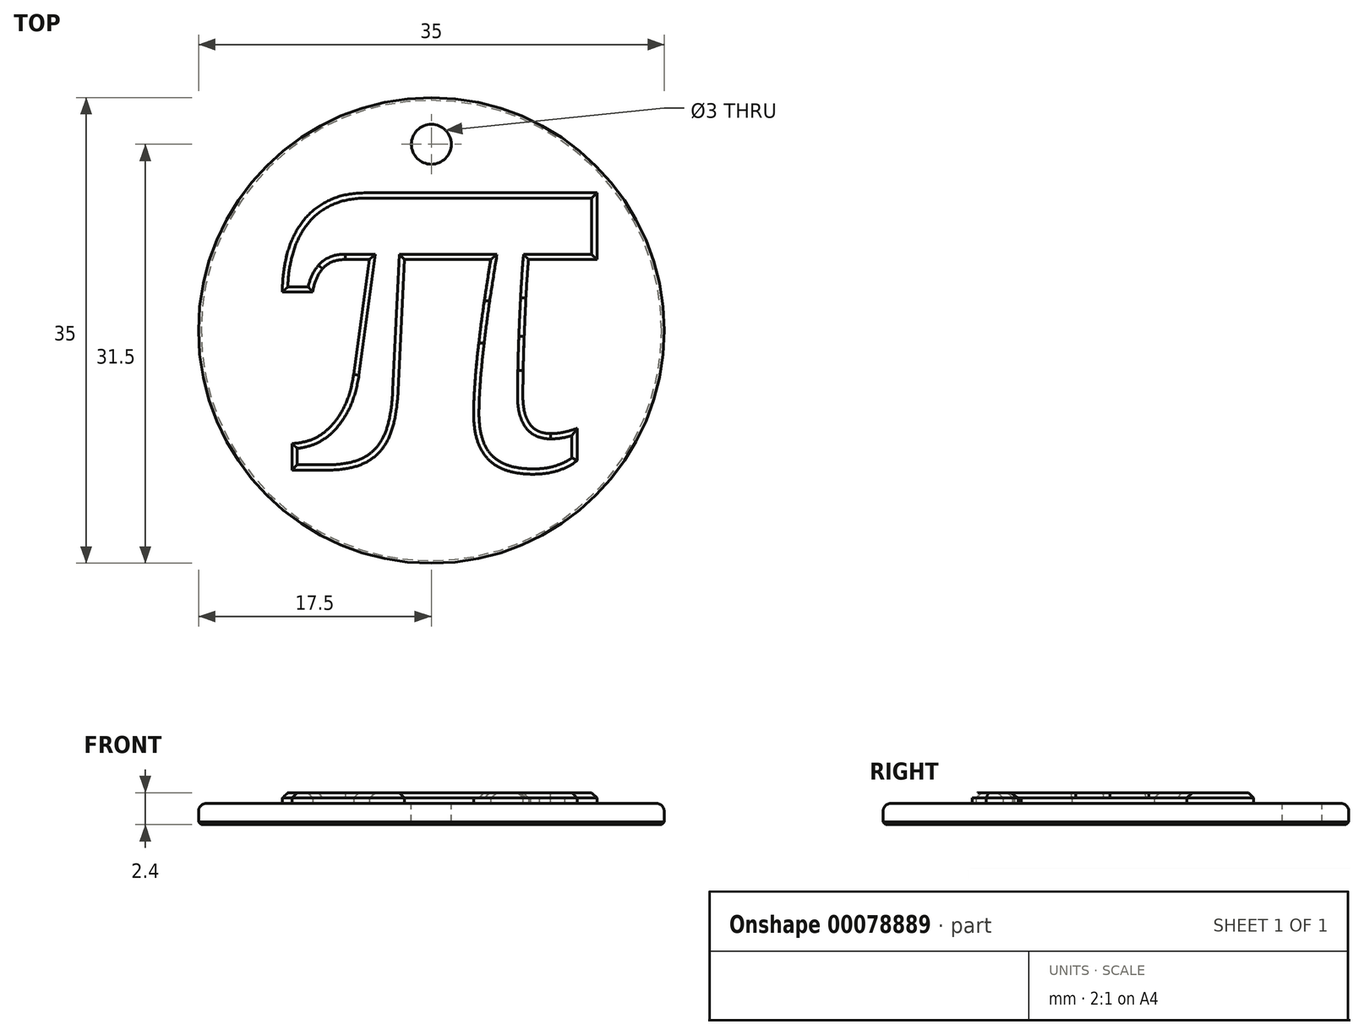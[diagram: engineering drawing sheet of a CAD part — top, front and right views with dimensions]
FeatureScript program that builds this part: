
annotation { "Feature Type Name" : "Feature", "Feature Type Description" : "" }
export const myFeature = defineFeature(function(context is Context, id is Id, definition is map)
    precondition{}
    {
        {
            var Q0;
            Q0=qCreatedBy(makeId("Top.planeOp"),FACE);
            var sketch = newSketch(context, id + "F0", { "sketchPlane" : qUnion([Q0])});
            skText(sketch, "E0", { "text": "π", "fontName": "NotoSerif-Bold.ttf"});
            skPoint(sketch, "E1", {"position": v(0, 3.5) * mm});
            skCircle(sketch, "E2", {"center": v(0, 0) * mm, "radius": 17.5 * mm});
            const initialGuessF0  = {"E0": [-0.01245, -0.0105, 1, 0, 0.028]};
            skSetInitialGuess(sketch, initialGuessF0);
            skSolve(sketch);
        }
        {
            var Q0;
            Q0 = qSketchRegion(id + "F0", true);
            var Q1;
            Q1=makeQuery(id+"F0.imprint","IMPRINT",FACE,{"disambiguationData":[TD([[makeQuery(id+"F0.imprint","IMPRINT",EDGE,{"derivedFrom":sQuery(id+"F0.wireOp",EDGE,"E0.sketch_text.stroke-0")}),-1.0]])]});
            extrude(context, id + "F1", {"entities" : qUnion([Q0, Q1]), "depth" : 1.6 * mm});
        }
        {
            var Q0;
            Q0=makeQuery(id+"F0.imprint","IMPRINT",FACE,{"disambiguationData":[TD([[makeQuery(id+"F0.imprint","IMPRINT",EDGE,{"derivedFrom":sQuery(id+"F0.wireOp",EDGE,"E0.sketch_text.stroke-0")}),-1.0]])]});
            extrude(context, id + "F2", {"entities" : qUnion([Q0]), "operationType" : NewBodyOperationType.ADD, "depth" : 2.4 * mm});
        }
        {
            var Q0;
            Q0=makeQuery(id+"F1.opExtrude","CAP_FACE",FACE,{"disambiguationData":[OSD([sQuery(id+"F0.wireOp",EDGE,"E2")])],"isStart":false});
            var sketch = newSketch(context, id + "F3", { "sketchPlane" : qUnion([Q0])});
            skCircle(sketch, "E3", {"center": v(0, 14) * mm, "radius": 1.5 * mm});
            skLineSegment(sketch, "E4", {"start": v(-7.86, 17.5) * mm, "end": v(8.67, 17.5) * mm, "construction": true});
            skSolve(sketch);
        }
        {
            var Q0;
            Q0=makeQuery(id+"F3.imprint","IMPRINT",FACE,{"disambiguationData":[TD([[makeQuery(id+"F3.imprint","IMPRINT",EDGE,{"derivedFrom":sQuery(id+"F3.wireOp",EDGE,"E3")}),1.0]])]});
            extrude(context, id + "F4", {"entities" : qUnion([Q0]), "operationType" : NewBodyOperationType.REMOVE, "endBound" : BoundingType.THROUGH_ALL, "oppositeDirection" : true, "depth" : 25 * mm});
        }
        {
            var Q0;
            Q0=makeQuery(id+"F4.boolean.opBoolean","COPY",EDGE,{"derivedFrom":makeQuery(id+"F4.opExtrude","CAP_EDGE",EDGE,{"disambiguationData":[OSD([sQuery(id+"F3.wireOp",EDGE,"E3")])],"isStart":true})});
            var Q1;
            Q1=makeQuery(id+"F1.opExtrude","CAP_EDGE",EDGE,{"disambiguationData":[OSD([sQuery(id+"F0.wireOp",EDGE,"E2")])],"isStart":false});
            fillet(context, id + "F5", {"entities" : qUnion([Q0, Q1]), "radius" : 0.6 * mm, "tangentPropagation" : true, "allowEdgeOverflow" : false});
        }
        {
            var Q0;
            Q0=makeQuery(id+"F2.opExtrude","CAP_FACE",FACE,{"disambiguationData":[OSD([sQuery(id+"F0.wireOp",EDGE,"E0.sketch_text.stroke-0"),sQuery(id+"F0.wireOp",EDGE,"E0.sketch_text.stroke-1"),sQuery(id+"F0.wireOp",EDGE,"E0.sketch_text.stroke-2"),sQuery(id+"F0.wireOp",EDGE,"E0.sketch_text.stroke-3"),sQuery(id+"F0.wireOp",EDGE,"E0.sketch_text.stroke-4"),sQuery(id+"F0.wireOp",EDGE,"E0.sketch_text.stroke-5"),sQuery(id+"F0.wireOp",EDGE,"E0.sketch_text.stroke-6"),sQuery(id+"F0.wireOp",EDGE,"E0.sketch_text.stroke-7"),sQuery(id+"F0.wireOp",EDGE,"E0.sketch_text.stroke-8"),sQuery(id+"F0.wireOp",EDGE,"E0.sketch_text.stroke-9"),sQuery(id+"F0.wireOp",EDGE,"E0.sketch_text.stroke-10"),sQuery(id+"F0.wireOp",EDGE,"E0.sketch_text.stroke-11"),sQuery(id+"F0.wireOp",EDGE,"E0.sketch_text.stroke-12"),sQuery(id+"F0.wireOp",EDGE,"E0.sketch_text.stroke-13"),sQuery(id+"F0.wireOp",EDGE,"E0.sketch_text.stroke-14"),sQuery(id+"F0.wireOp",EDGE,"E0.sketch_text.stroke-15"),sQuery(id+"F0.wireOp",EDGE,"E0.sketch_text.stroke-16"),sQuery(id+"F0.wireOp",EDGE,"E0.sketch_text.stroke-17"),sQuery(id+"F0.wireOp",EDGE,"E0.sketch_text.stroke-18"),sQuery(id+"F0.wireOp",EDGE,"E0.sketch_text.stroke-19"),sQuery(id+"F0.wireOp",EDGE,"E0.sketch_text.stroke-20"),sQuery(id+"F0.wireOp",EDGE,"E0.sketch_text.stroke-21"),sQuery(id+"F0.wireOp",EDGE,"E0.sketch_text.stroke-22"),sQuery(id+"F0.wireOp",EDGE,"E0.sketch_text.stroke-23"),sQuery(id+"F0.wireOp",EDGE,"E0.sketch_text.stroke-24"),sQuery(id+"F0.wireOp",EDGE,"E0.sketch_text.stroke-25"),sQuery(id+"F0.wireOp",EDGE,"E0.sketch_text.stroke-26"),sQuery(id+"F0.wireOp",EDGE,"E0.sketch_text.stroke-27"),sQuery(id+"F0.wireOp",EDGE,"E0.sketch_text.stroke-28"),sQuery(id+"F0.wireOp",EDGE,"E0.sketch_text.stroke-29"),sQuery(id+"F0.wireOp",EDGE,"E0.sketch_text.stroke-30"),sQuery(id+"F0.wireOp",EDGE,"E0.sketch_text.stroke-31"),sQuery(id+"F0.wireOp",EDGE,"E0.sketch_text.stroke-32"),sQuery(id+"F0.wireOp",EDGE,"E0.sketch_text.stroke-33"),sQuery(id+"F0.wireOp",EDGE,"E0.sketch_text.stroke-34"),sQuery(id+"F0.wireOp",EDGE,"E0.sketch_text.stroke-35"),sQuery(id+"F0.wireOp",EDGE,"E0.sketch_text.stroke-36"),sQuery(id+"F0.wireOp",EDGE,"E0.sketch_text.stroke-37"),sQuery(id+"F0.wireOp",EDGE,"E0.sketch_text.stroke-38"),sQuery(id+"F0.wireOp",EDGE,"E0.sketch_text.stroke-39"),sQuery(id+"F0.wireOp",EDGE,"E0.sketch_text.stroke-40"),sQuery(id+"F0.wireOp",EDGE,"E0.sketch_text.stroke-41"),sQuery(id+"F0.wireOp",EDGE,"E0.sketch_text.stroke-42"),sQuery(id+"F0.wireOp",EDGE,"E0.sketch_text.stroke-43"),sQuery(id+"F0.wireOp",EDGE,"E0.sketch_text.stroke-44")])],"isStart":false});
            chamfer(context, id + "F6", {"entities" : qUnion([Q0]), "width" : 0.4 * mm, "tangentPropagation" : true});
        }
        {
            var Q0;
            Q0=makeQuery(id+"F1.opExtrude","CAP_EDGE",EDGE,{"disambiguationData":[OSD([sQuery(id+"F0.wireOp",EDGE,"E2")])],"isStart":true});
            chamfer(context, id + "F7", {"entities" : qUnion([Q0]), "width" : 0.2 * mm, "tangentPropagation" : true});
        }
    });
